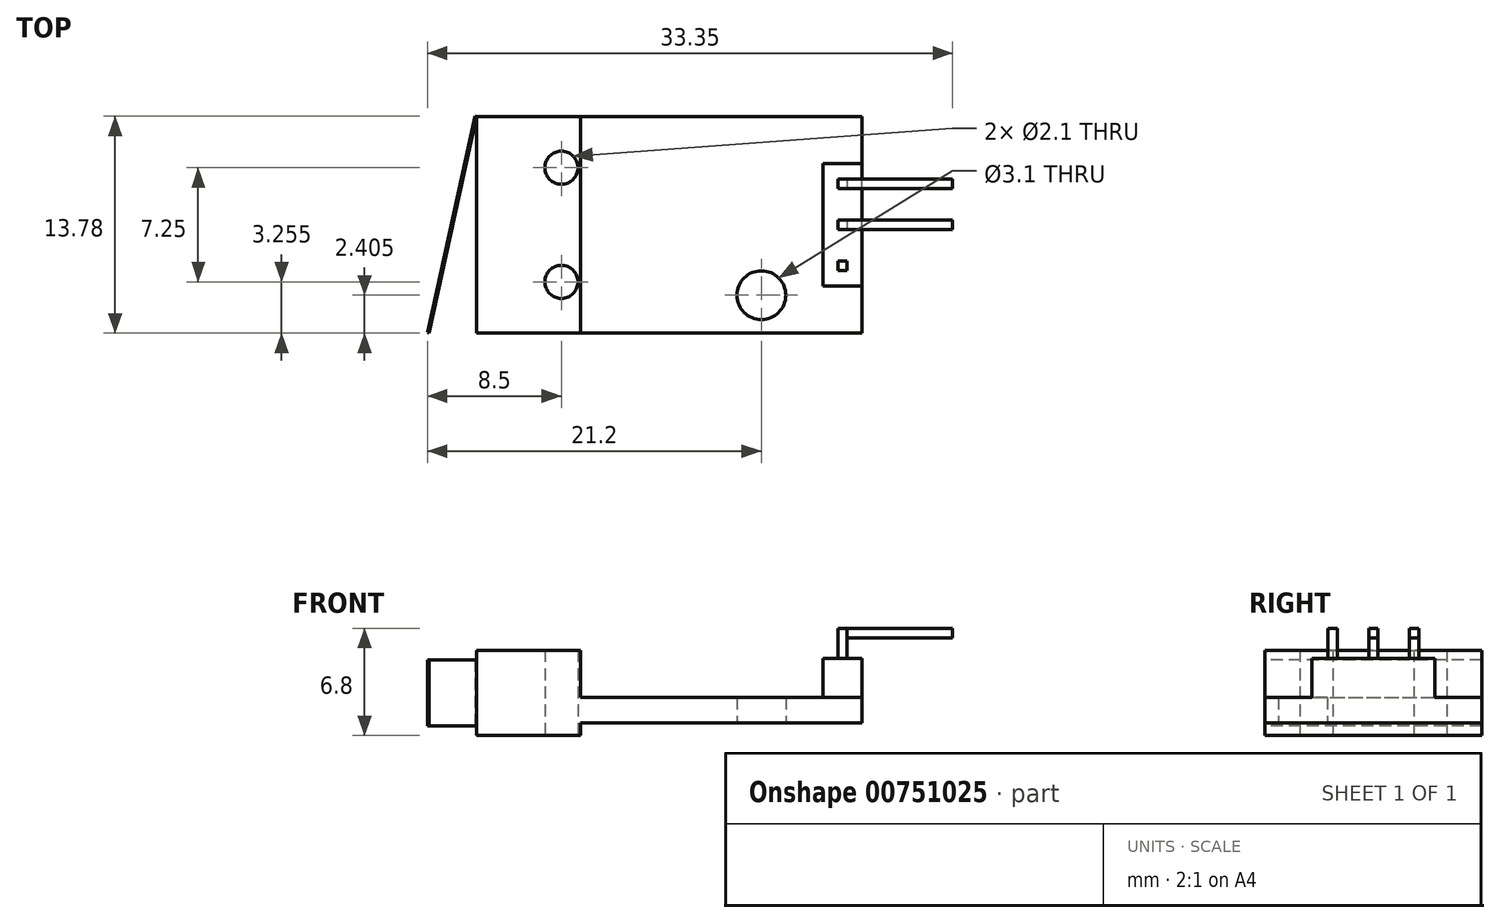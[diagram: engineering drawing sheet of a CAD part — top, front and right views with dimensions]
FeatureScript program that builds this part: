
annotation { "Feature Type Name" : "Feature", "Feature Type Description" : "" }
export const myFeature = defineFeature(function(context is Context, id is Id, definition is map)
    precondition{}
    {
        {
            var Q0;
            Q0=qCreatedBy(makeId("Top.planeOp"),FACE);
            var sketch = newSketch(context, id + "F0", { "sketchPlane" : qUnion([Q0])});
            skLineSegment(sketch, "E0.bottom", {"start": v(8.95, -6.88) * mm, "end": v(-8.95, -6.88) * mm});
            skLineSegment(sketch, "E0.top", {"start": v(8.95, 6.88) * mm, "end": v(-8.95, 6.88) * mm});
            skLineSegment(sketch, "E0.left", {"start": v(8.95, -6.88) * mm, "end": v(8.95, 6.87) * mm});
            skLineSegment(sketch, "E0.right", {"start": v(-8.95, -6.88) * mm, "end": v(-8.95, 6.87) * mm});
            skPoint(sketch, "E0.middle", {"position": v(0, 0) * mm});
            skLineSegment(sketch, "E1.bottom", {"start": v(8.95, 3.9) * mm, "end": v(6.45, 3.9) * mm});
            skLineSegment(sketch, "E1.top", {"start": v(8.95, -3.9) * mm, "end": v(6.45, -3.9) * mm});
            skLineSegment(sketch, "E1.left", {"start": v(8.95, 3.9) * mm, "end": v(8.95, -3.9) * mm});
            skLineSegment(sketch, "E1.right", {"start": v(6.45, 3.9) * mm, "end": v(6.45, -3.9) * mm});
            skLineSegment(sketch, "E2", {"start": v(8.95, 6.88) * mm, "end": v(8.95, 3.9) * mm});
            skLineSegment(sketch, "E3", {"start": v(8.95, -3.9) * mm, "end": v(8.95, -6.88) * mm});
            skLineSegment(sketch, "E4", {"start": v(6.45, 1.3) * mm, "end": v(8.95, 1.3) * mm});
            skLineSegment(sketch, "E5", {"start": v(6.45, -1.3) * mm, "end": v(8.95, -1.3) * mm});
            skLineSegment(sketch, "E6", {"start": v(8.95, 3.9) * mm, "end": v(8.95, 1.3) * mm});
            skLineSegment(sketch, "E7", {"start": v(8.95, -1.3) * mm, "end": v(8.95, -3.9) * mm});
            skLineSegment(sketch, "E8", {"start": v(8.95, 1.3) * mm, "end": v(8.95, -1.3) * mm});
            skLineSegment(sketch, "E9.bottom", {"start": v(-8.95, 6.88) * mm, "end": v(-15.55, 6.88) * mm});
            skLineSegment(sketch, "E9.top", {"start": v(-8.95, -6.88) * mm, "end": v(-15.55, -6.88) * mm});
            skLineSegment(sketch, "E9.left", {"start": v(-8.95, 6.88) * mm, "end": v(-8.95, -6.88) * mm});
            skLineSegment(sketch, "E9.right", {"start": v(-15.55, 6.87) * mm, "end": v(-15.55, -6.88) * mm});
            skLineSegment(sketch, "E10", {"start": v(7.7, 3.9) * mm, "end": v(7.7, 1.3) * mm, "construction": true});
            skLineSegment(sketch, "E11", {"start": v(7.7, 1.3) * mm, "end": v(7.7, -1.3) * mm, "construction": true});
            skLineSegment(sketch, "E12", {"start": v(7.7, -1.3) * mm, "end": v(7.7, -3.9) * mm, "construction": true});
            skLineSegment(sketch, "E13.bottom", {"start": v(8, 2.3) * mm, "end": v(7.4, 2.3) * mm});
            skLineSegment(sketch, "E13.top", {"start": v(8, 2.9) * mm, "end": v(7.4, 2.9) * mm});
            skLineSegment(sketch, "E13.left", {"start": v(8, 2.3) * mm, "end": v(8, 2.9) * mm});
            skLineSegment(sketch, "E13.right", {"start": v(7.4, 2.3) * mm, "end": v(7.4, 2.9) * mm});
            skPoint(sketch, "E13.middle", {"position": v(7.7, 2.6) * mm});
            skLineSegment(sketch, "E14.bottom", {"start": v(8, -0.3) * mm, "end": v(7.4, -0.3) * mm});
            skLineSegment(sketch, "E14.top", {"start": v(8, 0.3) * mm, "end": v(7.4, 0.3) * mm});
            skLineSegment(sketch, "E14.left", {"start": v(8, -0.3) * mm, "end": v(8, 0.3) * mm});
            skLineSegment(sketch, "E14.right", {"start": v(7.4, -0.3) * mm, "end": v(7.4, 0.3) * mm});
            skPoint(sketch, "E14.middle", {"position": v(7.7, 0) * mm});
            skLineSegment(sketch, "E15.bottom", {"start": v(8, -2.9) * mm, "end": v(7.4, -2.9) * mm});
            skLineSegment(sketch, "E15.top", {"start": v(8, -2.3) * mm, "end": v(7.4, -2.3) * mm});
            skLineSegment(sketch, "E15.left", {"start": v(8, -2.9) * mm, "end": v(8, -2.3) * mm});
            skLineSegment(sketch, "E15.right", {"start": v(7.4, -2.9) * mm, "end": v(7.4, -2.3) * mm});
            skPoint(sketch, "E15.middle", {"position": v(7.7, -2.6) * mm});
            skLineSegment(sketch, "E16", {"start": v(-15.55, 6.88) * mm, "end": v(-18.55, -6.88) * mm});
            skLineSegment(sketch, "E17.0", {"start": v(-15.65, 6.9) * mm, "end": v(-18.65, -6.85) * mm});
            skLineSegment(sketch, "E18", {"start": v(-15.65, 6.9) * mm, "end": v(-15.55, 6.87) * mm});
            skLineSegment(sketch, "E19", {"start": v(-18.65, -6.85) * mm, "end": v(-18.55, -6.88) * mm});
            skLineSegment(sketch, "E20.right", {"start": v(-15.55, 6.88) * mm, "end": v(-15.55, -6.88) * mm});
            skCircle(sketch, "E21", {"center": v(-10.15, -3.63) * mm, "radius": 1.05 * mm});
            skCircle(sketch, "E22", {"center": v(-10.15, 3.62) * mm, "radius": 1.05 * mm});
            skLineSegment(sketch, "E23", {"start": v(-10.15, -4.68) * mm, "end": v(-8.95, -4.68) * mm});
            skLineSegment(sketch, "E24", {"start": v(-10.15, 4.67) * mm, "end": v(-8.95, 4.67) * mm});
            skLineSegment(sketch, "E25", {"start": v(-8.95, -6.88) * mm, "end": v(-8.95, 4.67) * mm});
            skLineSegment(sketch, "E26", {"start": v(-8.95, -4.68) * mm, "end": v(-8.95, 6.88) * mm});
            skCircle(sketch, "E27", {"center": v(2.55, -4.48) * mm, "radius": 1.55 * mm});
            skLineSegment(sketch, "E28", {"start": v(2.55, -4.48) * mm, "end": v(2.55, -6.88) * mm, "construction": true});
            skLineSegment(sketch, "E29", {"start": v(2.55, -4.54) * mm, "end": v(8.95, -4.54) * mm, "construction": true});
            skSolve(sketch);
        }
        {
            var Q0;
            {var subQ8=sQuery(id+"F0.wireOp",EDGE,"E0.bottom");Q0=makeQuery(id+"F0.imprint","IMPRINT",FACE,{"disambiguationData":[TD([[makeQuery(id+"F0.imprint","IMPRINT",EDGE,{"derivedFrom":subQ8}),-1.0]])]});}
            var Q1;
            {var subQ2=sQuery(id+"F0.wireOp",EDGE,"E1.bottom");Q1=makeQuery(id+"F0.imprint","IMPRINT",FACE,{"disambiguationData":[TD([[makeQuery(id+"F0.imprint","IMPRINT",EDGE,{"derivedFrom":subQ2}),1.0]])]});}
            var Q2;
            {var subQ0=sQuery(id+"F0.wireOp",EDGE,"E4");Q2=makeQuery(id+"F0.imprint","IMPRINT",FACE,{"disambiguationData":[TD([[makeQuery(id+"F0.imprint","IMPRINT",EDGE,{"derivedFrom":subQ0}),-1.0]])]});}
            var Q3;
            Q3=makeQuery(id+"F0.imprint","IMPRINT",FACE,{"disambiguationData":[TD([[makeQuery(id+"F0.imprint","IMPRINT",EDGE,{"derivedFrom":sQuery(id+"F0.wireOp",EDGE,"E13.bottom")}),-1.0]])]});
            var Q4;
            Q4=makeQuery(id+"F0.imprint","IMPRINT",FACE,{"disambiguationData":[TD([[makeQuery(id+"F0.imprint","IMPRINT",EDGE,{"derivedFrom":sQuery(id+"F0.wireOp",EDGE,"E14.bottom")}),-1.0]])]});
            var Q5;
            {var subQ2=sQuery(id+"F0.wireOp",EDGE,"E1.top");Q5=makeQuery(id+"F0.imprint","IMPRINT",FACE,{"disambiguationData":[TD([[makeQuery(id+"F0.imprint","IMPRINT",EDGE,{"derivedFrom":subQ2}),-1.0]])]});}
            var Q6;
            Q6=makeQuery(id+"F0.imprint","IMPRINT",FACE,{"disambiguationData":[TD([[makeQuery(id+"F0.imprint","IMPRINT",EDGE,{"derivedFrom":sQuery(id+"F0.wireOp",EDGE,"E15.bottom")}),-1.0]])]});
            extrude(context, id + "F1", {"entities" : qUnion([Q0, Q1, Q2, Q3, Q4, Q5, Q6]), "depth" : 1.6 * mm, "offsetDistance" : 25 * mm});
        }
        {
            var Q0;
            Q0=makeQuery(id+"F0.imprint","IMPRINT",FACE,{"disambiguationData":[TD([[makeQuery(id+"F0.imprint","IMPRINT",EDGE,{"derivedFrom":sQuery(id+"F0.wireOp",EDGE,"E13.bottom")}),-1.0]])]});
            var Q1;
            {var subQ2=sQuery(id+"F0.wireOp",EDGE,"E1.bottom");Q1=makeQuery(id+"F0.imprint","IMPRINT",FACE,{"disambiguationData":[TD([[makeQuery(id+"F0.imprint","IMPRINT",EDGE,{"derivedFrom":subQ2}),1.0]])]});}
            var Q2;
            Q2=makeQuery(id+"F0.imprint","IMPRINT",FACE,{"disambiguationData":[TD([[makeQuery(id+"F0.imprint","IMPRINT",EDGE,{"derivedFrom":sQuery(id+"F0.wireOp",EDGE,"E14.bottom")}),-1.0]])]});
            var Q3;
            {var subQ0=sQuery(id+"F0.wireOp",EDGE,"E4");Q3=makeQuery(id+"F0.imprint","IMPRINT",FACE,{"disambiguationData":[TD([[makeQuery(id+"F0.imprint","IMPRINT",EDGE,{"derivedFrom":subQ0}),-1.0]])]});}
            var Q4;
            Q4=makeQuery(id+"F0.imprint","IMPRINT",FACE,{"disambiguationData":[TD([[makeQuery(id+"F0.imprint","IMPRINT",EDGE,{"derivedFrom":sQuery(id+"F0.wireOp",EDGE,"E15.bottom")}),-1.0]])]});
            var Q5;
            {var subQ2=sQuery(id+"F0.wireOp",EDGE,"E1.top");Q5=makeQuery(id+"F0.imprint","IMPRINT",FACE,{"disambiguationData":[TD([[makeQuery(id+"F0.imprint","IMPRINT",EDGE,{"derivedFrom":subQ2}),-1.0]])]});}
            extrude(context, id + "F2", {"entities" : qUnion([Q0, Q1, Q2, Q3, Q4, Q5]), "operationType" : NewBodyOperationType.ADD, "depth" : (2.5 + 1.6) * mm, "offsetDistance" : 25 * mm});
        }
        {
            var Q0;
            Q0=makeQuery(id+"F0.imprint","IMPRINT",FACE,{"disambiguationData":[TD([[makeQuery(id+"F0.imprint","IMPRINT",EDGE,{"derivedFrom":sQuery(id+"F0.wireOp",EDGE,"E15.bottom")}),-1.0]])]});
            var Q1;
            Q1=makeQuery(id+"F0.imprint","IMPRINT",FACE,{"disambiguationData":[TD([[makeQuery(id+"F0.imprint","IMPRINT",EDGE,{"derivedFrom":sQuery(id+"F0.wireOp",EDGE,"E14.bottom")}),-1.0]])]});
            var Q2;
            Q2=makeQuery(id+"F0.imprint","IMPRINT",FACE,{"disambiguationData":[TD([[makeQuery(id+"F0.imprint","IMPRINT",EDGE,{"derivedFrom":sQuery(id+"F0.wireOp",EDGE,"E13.bottom")}),-1.0]])]});
            extrude(context, id + "F3", {"entities" : qUnion([Q0, Q1, Q2]), "operationType" : NewBodyOperationType.ADD, "depth" : 6 * mm, "offsetDistance" : 25 * mm});
        }
        {
            var Q0;
            Q0=makeQuery(id+"F3.opExtrude","SWEPT_FACE",FACE,{"disambiguationData":[OSD([sQuery(id+"F0.wireOp",EDGE,"E15.left")])]});
            var sketch = newSketch(context, id + "F4", { "sketchPlane" : qUnion([Q0])});
            skLineSegment(sketch, "E30.0.0", {"start": v(-2.9, 4.1) * mm, "end": v(-2.3, 4.1) * mm});
            skLineSegment(sketch, "E30.0.1", {"start": v(-2.3, 4.1) * mm, "end": v(-2.3, 6) * mm});
            skLineSegment(sketch, "E30.0.2", {"start": v(-2.3, 6) * mm, "end": v(-2.9, 6) * mm});
            skLineSegment(sketch, "E30.0.3", {"start": v(-2.9, 6) * mm, "end": v(-2.9, 4.1) * mm});
            skLineSegment(sketch, "E31.0.0", {"start": v(-0.3, 4.1) * mm, "end": v(0.3, 4.1) * mm});
            skLineSegment(sketch, "E31.0.1", {"start": v(0.3, 4.1) * mm, "end": v(0.3, 6) * mm});
            skLineSegment(sketch, "E31.0.2", {"start": v(0.3, 6) * mm, "end": v(-0.3, 6) * mm});
            skLineSegment(sketch, "E31.0.3", {"start": v(-0.3, 6) * mm, "end": v(-0.3, 4.1) * mm});
            skLineSegment(sketch, "E32.0.0", {"start": v(2.3, 4.1) * mm, "end": v(2.9, 4.1) * mm});
            skLineSegment(sketch, "E32.0.1", {"start": v(2.9, 4.1) * mm, "end": v(2.9, 6) * mm});
            skLineSegment(sketch, "E32.0.2", {"start": v(2.9, 6) * mm, "end": v(2.3, 6) * mm});
            skLineSegment(sketch, "E32.0.3", {"start": v(2.3, 6) * mm, "end": v(2.3, 4.1) * mm});
            skLineSegment(sketch, "E33.bottom", {"start": v(-2.9, 6) * mm, "end": v(-2.3, 6) * mm});
            skLineSegment(sketch, "E33.top", {"start": v(-2.9, 5.4) * mm, "end": v(-2.3, 5.4) * mm});
            skLineSegment(sketch, "E33.left", {"start": v(-2.9, 6) * mm, "end": v(-2.9, 5.4) * mm});
            skLineSegment(sketch, "E33.right", {"start": v(-2.3, 6) * mm, "end": v(-2.3, 5.4) * mm});
            skLineSegment(sketch, "E34.top", {"start": v(0.3, 5.4) * mm, "end": v(-0.3, 5.4) * mm});
            skLineSegment(sketch, "E34.left", {"start": v(0.3, 6) * mm, "end": v(0.3, 5.4) * mm});
            skLineSegment(sketch, "E34.right", {"start": v(-0.3, 6) * mm, "end": v(-0.3, 5.4) * mm});
            skLineSegment(sketch, "E35.top", {"start": v(2.9, 5.4) * mm, "end": v(2.3, 5.4) * mm});
            skLineSegment(sketch, "E35.left", {"start": v(2.9, 6) * mm, "end": v(2.9, 5.4) * mm});
            skLineSegment(sketch, "E35.right", {"start": v(2.3, 6) * mm, "end": v(2.3, 5.4) * mm});
            skSolve(sketch);
        }
        {
            var Q0;
            Q0=makeQuery(id+"F4.imprint","IMPRINT",FACE,{"disambiguationData":[TD([[makeQuery(id+"F4.imprint","IMPRINT",EDGE,{"derivedFrom":sQuery(id+"F4.wireOp",EDGE,"E33.bottom")}),-1.0]])]});
            var Q1;
            Q1=makeQuery(id+"F4.imprint","IMPRINT",FACE,{"disambiguationData":[TD([[makeQuery(id+"F4.imprint","IMPRINT",EDGE,{"derivedFrom":sQuery(id+"F4.wireOp",EDGE,"E31.0.2")}),1.0]])]});
            var Q2;
            Q2=makeQuery(id+"F4.imprint","IMPRINT",FACE,{"disambiguationData":[TD([[makeQuery(id+"F4.imprint","IMPRINT",EDGE,{"derivedFrom":sQuery(id+"F4.wireOp",EDGE,"E32.0.2")}),1.0]])]});
            extrude(context, id + "F5", {"entities" : qUnion([Q0, Q1, Q2]), "operationType" : NewBodyOperationType.ADD, "depth" : 6.7 * mm, "offsetDistance" : 25 * mm});
        }
        {
            var Q0;
            {var subQ0=sQuery(id+"F0.wireOp",EDGE,"E9.bottom");Q0=makeQuery(id+"F0.imprint","IMPRINT",FACE,{"disambiguationData":[TD([[makeQuery(id+"F0.imprint","IMPRINT",EDGE,{"derivedFrom":subQ0}),1.0]])]});}
            extrude(context, id + "F6", {"entities" : qUnion([Q0]), "operationType" : NewBodyOperationType.ADD, "depth" : (3 + 1.6) * mm, "offsetDistance" : 25 * mm});
        }
        {
            var Q0;
            {var subQ0=sQuery(id+"F0.wireOp",EDGE,"E9.bottom");Q0=makeQuery(id+"F0.imprint","IMPRINT",FACE,{"disambiguationData":[TD([[makeQuery(id+"F0.imprint","IMPRINT",EDGE,{"derivedFrom":subQ0}),1.0]])]});}
            extrude(context, id + "F7", {"entities" : qUnion([Q0]), "operationType" : NewBodyOperationType.ADD, "oppositeDirection" : true, "depth" : 0.8 * mm, "offsetDistance" : 25 * mm});
        }
        {
            var Q0;
            Q0=makeQuery(id+"F0.imprint","IMPRINT",FACE,{"disambiguationData":[TD([[makeQuery(id+"F0.imprint","IMPRINT",EDGE,{"derivedFrom":sQuery(id+"F0.wireOp",EDGE,"E16")}),-1.0]])]});
            extrude(context, id + "F8", {"entities" : qUnion([Q0]), "depth" : 4 * mm, "offsetDistance" : 25 * mm, "hasSecondDirection" : true, "secondDirectionOppositeDirection" : true, "secondDirectionDepth" : 0.2 * mm});
        }
    });
